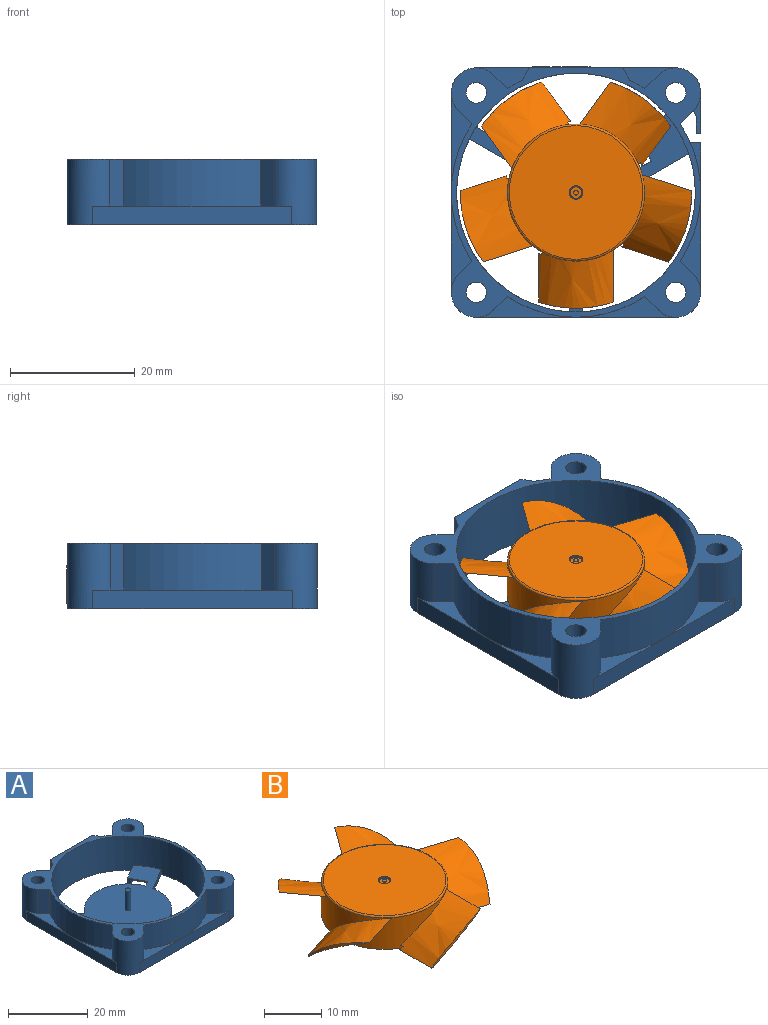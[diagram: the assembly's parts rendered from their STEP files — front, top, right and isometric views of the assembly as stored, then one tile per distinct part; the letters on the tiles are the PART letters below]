
ASSEMBLY  parts=2 mates=1
PART A: 78 faces, bbox 40x40.2x10.5 mm
  f0: plane 32x10.5mm, normal (0,1,0), area 191.9mm2, adj f9,f10,f13,f18,f19,f38,f60,f61
  f1: cylinder r=20mm len=7.5mm, axis (0,0,-1), area 20.7mm2, adj f10,f29,f38,f60
  f2: plane 35.21x31.71mm, normal (0,0,1), area 463mm2, adj f25,f39,f40,f41,f42,f43,f44,f45
  f3: plane 7.98x1.66mm, normal (0,0,1), area 4.3mm2, adj f4,f27,f54
  f4: plane 23.98x3mm, normal (1,0,0), area 71.9mm2, adj f3,f11,f13,f16,f54
  f5: plane 16x3.32mm, normal (0,0,1), area 17.6mm2, adj f15,f16,f36,f37
  f6: plane 16x3.32mm, normal (0,0,1), area 17.6mm2, adj f14,f15,f35,f36
  f7: plane 16x3.32mm, normal (0,0,1), area 17.6mm2, adj f14,f20,f33,f34
  f8: plane 16x3.32mm, normal (0,0,1), area 17.6mm2, adj f19,f20,f32,f33
  f9: plane 8.5x3.32mm, normal (0,0,1), area 13.2mm2, adj f0,f19,f30,f31,f61
  f10: plane 8.5x3.32mm, normal (0,0,1), area 13.2mm2, adj f0,f1,f18,f29,f60
  f11: plane 16x3.32mm, normal (0,0,1), area 17.6mm2, adj f4,f16,f26,f27
  f12: plane 6.52x1.17mm, normal (0,0,1), area 3.8mm2, adj f17,f18,f55,f56,f57
  f13: plane 40x40mm, normal (0,0,-1), area 825.1mm2, adj f0,f4,f14,f15,f16,f17,f18,f19
  f14: cylinder r=4mm len=10.5mm, axis (0,0,-1), area 113.1mm2, adj f6,f7,f13,f15,f20,f34,f35,f38
  f15: plane 32x3mm, normal (0,-1,0), area 96mm2, adj f5,f6,f13,f14,f16
  f16: cylinder r=4mm len=10.5mm, axis (0,0,-1), area 113.1mm2, adj f4,f5,f11,f13,f15,f26,f37,f38
  f17: plane 6.52x3mm, normal (1,0,0), area 19.6mm2, adj f12,f13,f18,f55
  f18: cylinder r=4mm len=10.5mm, axis (0,0,-1), area 113.1mm2, adj f0,f10,f12,f13,f17,f28,f29,f38
  f19: cylinder r=4mm len=10.5mm, axis (0,0,-1), area 113.1mm2, adj f0,f8,f9,f13,f20,f31,f32,f38
  f20: plane 32x3mm, normal (-1,0,0), area 96mm2, adj f7,f8,f13,f14,f19
  f21: cylinder r=1.65mm len=10.5mm, axis (0,0,-1), area 108.9mm2, adj f13,f38
  f22: cylinder r=1.65mm len=10.5mm, axis (0,0,-1), area 108.9mm2, adj f13,f38
  f23: cylinder r=1.65mm len=10.5mm, axis (0,0,-1), area 108.9mm2, adj f13,f38
  f24: cylinder r=1.65mm len=10.5mm, axis (0,0,-1), area 108.9mm2, adj f13,f38
  f25: cylinder r=19.15mm len=38.3mm, axis (0,0,-1), area 1245.8mm2, adj f2,f13,f38,f40,f41,f43,f44,f46
  f26: plane 7.5x2.14mm, normal (0.71,0.71,0), area 22.7mm2, adj f11,f16,f27,f38
  f27: cylinder r=20mm len=22.06mm, axis (0,0,-1), area 181.8mm2, adj f3,f11,f26,f28,f38,f53,f54
  f28: plane 10.5x2.14mm, normal (0.71,-0.71,0), area 31.8mm2, adj f13,f18,f27,f38,f51,f57
  f29: plane 7.5x2.14mm, normal (-0.71,0.71,0), area 22.7mm2, adj f1,f10,f18,f38
  f30: cylinder r=20mm len=7.5mm, axis (0,0,-1), area 20.7mm2, adj f9,f31,f38,f61
  f31: plane 7.5x2.14mm, normal (0.71,0.71,0), area 22.7mm2, adj f9,f19,f30,f38
  f32: plane 7.5x2.14mm, normal (-0.71,-0.71,0), area 22.7mm2, adj f8,f19,f33,f38
  f33: cylinder r=20mm len=22.06mm, axis (0,0,-1), area 175.2mm2, adj f7,f8,f32,f34,f38
  f34: plane 7.5x2.14mm, normal (-0.71,0.71,0), area 22.7mm2, adj f7,f14,f33,f38
  f35: plane 7.5x2.14mm, normal (0.71,-0.71,0), area 22.7mm2, adj f6,f14,f36,f38
  f36: cylinder r=20mm len=22.06mm, axis (0,0,-1), area 175.2mm2, adj f5,f6,f35,f37,f38
  f37: plane 7.5x2.14mm, normal (-0.71,-0.71,0), area 22.7mm2, adj f5,f16,f36,f38
  f38: plane 40x40mm, normal (0,0,1), area 268.1mm2, adj f0,f1,f14,f16,f18,f19,f21,f22
  f39: cylinder r=11mm len=15.46mm, axis (0,0,-1), area 31.3mm2, adj f2,f13,f40,f47
  f40: plane 8.17x1.5mm, normal (-1,0,0), area 12.3mm2, adj f2,f13,f25,f39
  f41: plane 8.17x1.5mm, normal (1,0,0), area 12.3mm2, adj f2,f13,f25,f42
  f42: cylinder r=11mm len=12.97mm, axis (0,0,-1), area 27.3mm2, adj f2,f13,f41,f43
  f43: plane 7.29x4.21mm, normal (0.5,-0.87,0), area 12.6mm2, adj f2,f13,f25,f42
  f44: plane 5.02x2.9mm, normal (-0.5,0.87,0), area 8.7mm2, adj f2,f13,f25,f49
  f45: cylinder r=11mm len=19.17mm, axis (0,0,-1), area 35.4mm2, adj f2,f13,f46,f48
  f46: plane 7.08x4.09mm, normal (0.5,0.87,0), area 12.3mm2, adj f2,f13,f25,f45
  f47: plane 7.08x4.09mm, normal (-0.5,-0.87,0), area 12.3mm2, adj f2,f13,f25,f39
  f48: plane 6.86x3.96mm, normal (-0.5,0.87,0), area 9.6mm2, adj f2,f13,f45,f49,f50,f53
  f49: plane 4.59x2.65mm, normal (-0.87,-0.5,0), area 3.2mm2, adj f2,f13,f44,f48,f52,f53
  f50: plane 1.23x1.1mm, normal (-0.01,1,0), area 1.4mm2, adj f13,f48,f53,f54
  f51: cylinder r=20mm len=1.18mm, axis (0,0,-1), area 1.6mm2, adj f13,f28,f52,f53
  f52: plane 5.91x3.41mm, normal (0.5,-0.87,0), area 7.5mm2, adj f13,f49,f51,f53
  f53: plane 8.41x7.14mm, normal (0,0,-1), area 30.3mm2, adj f27,f48,f49,f50,f51,f52
  f54: plane 3x1.66mm, normal (0,1,0), area 5mm2, adj f3,f4,f13,f27,f50
  f55: plane 3x0.7mm, normal (0,-1,0), area 2.1mm2, adj f12,f13,f17,f56
  f56: plane 3x2.73mm, normal (-1,0,0), area 8.2mm2, adj f12,f13,f55,f57
  f57: plane 3x0.96mm, normal (-0.9,-0.44,0), area 3.2mm2, adj f12,f13,f28,f56
  f58: cylinder r=0.75mm len=6mm, axis (0,0,-1), area 28.3mm2, adj f2,f59
  f59: plane 1.5x1.5mm, normal (0,0,1), area 1.8mm2, adj f58
  f60: plane 7.5x1.96mm, normal (0.87,0.5,0), area 17mm2, adj f0,f1,f10,f38
  f61: plane 7.5x1.96mm, normal (-0.87,0.5,0), area 17mm2, adj f0,f9,f30,f38
  f62: plane 1.4x0.2mm, normal (1,0,0), area 0.3mm2, adj f0,f63,f68,f69
  f63: plane 4x0.2mm, normal (0,0,-1), area 0.8mm2, adj f0,f62,f64,f69
  f64: plane 0.65x0.2mm, normal (1,0,0), area 0.1mm2, adj f0,f63,f65,f69
  f65: plane 2x1.35mm, normal (-0.56,0,-0.83), area 0.5mm2, adj f0,f64,f66,f69
  f66: plane 2x1.35mm, normal (-0.56,0,0.83), area 0.5mm2, adj f0,f65,f67,f69
  f67: plane 0.65x0.2mm, normal (1,0,0), area 0.1mm2, adj f0,f66,f68,f69
  f68: plane 4x0.2mm, normal (0,0,1), area 0.8mm2, adj f0,f62,f67,f69
  f69: plane 6x2.7mm, normal (0,1,0), area 8.3mm2, adj f62,f63,f64,f65,f66,f67,f68
  f70: plane 1.4x0.2mm, normal (0,0,1), area 0.3mm2, adj f0,f71,f76,f77
  f71: plane 4x0.2mm, normal (1,0,0), area 0.8mm2, adj f0,f70,f72,f77
  f72: plane 0.65x0.2mm, normal (0,0,1), area 0.1mm2, adj f0,f71,f73,f77
  f73: plane 2x1.35mm, normal (0.83,0,-0.56), area 0.5mm2, adj f0,f72,f74,f77
  f74: plane 2x1.35mm, normal (-0.83,0,-0.56), area 0.5mm2, adj f0,f73,f75,f77
  f75: plane 0.65x0.2mm, normal (0,0,1), area 0.1mm2, adj f0,f74,f76,f77
  f76: plane 4x0.2mm, normal (-1,0,0), area 0.8mm2, adj f0,f70,f75,f77
  f77: plane 6x2.7mm, normal (0,1,0), area 8.3mm2, adj f70,f71,f72,f73,f74,f75,f76
PART B: 45 faces, bbox 39x37.1x7 mm
  f0: plane 1.8x1.8mm, normal (0,0,1), area 2mm2, adj f32,f43
  f1: plane 22x22mm, normal (0,0,-1), area 66mm2, adj f6,f25
  f2: plane 7.66x2.66mm, normal (0,0,-1), area 2.3mm2, adj f12,f13,f14,f40
  f3: plane 6.62x4.76mm, normal (0,0,-1), area 2.3mm2, adj f15,f16,f17,f38
  f4: plane 6.39x4.92mm, normal (0,0,-1), area 2.3mm2, adj f18,f19,f20,f36
  f5: plane 7.48x2.75mm, normal (0,0,-1), area 2.3mm2, adj f21,f22,f23,f34
  f6: cylinder r=11mm len=22mm, axis (0,0,-1), area 435.1mm2, adj f1,f9,f10,f13,f14,f16,f17,f19
  f7: plane 21.4x21.4mm, normal (0,0,1), area 355.9mm2, adj f30,f31
  f8: plane 7.96x0.3mm, normal (0,0,-1), area 2.3mm2, adj f9,f10,f11,f41
  f9: extruded ~12x9.33mm, area 109.9mm2, adj f6,f8,f10,f11,f41,f42
  f10: extruded ~11.7x9.33mm, area 105.8mm2, adj f6,f8,f9,f11,f41,f42
  f11: cylinder r=18.55mm len=12mm, axis (0,0,-1), area 5.7mm2, adj f8,f9,f10
  f12: cylinder r=18.55mm len=11.41mm, axis (0,0,-1), area 5.7mm2, adj f2,f13,f14
  f13: extruded ~14.01x12.49mm, area 105.8mm2, adj f2,f6,f12,f14,f39,f40
  f14: extruded ~14.3x12.58mm, area 109.9mm2, adj f2,f6,f12,f13,f39,f40
  f15: cylinder r=18.55mm len=9.71mm, axis (0,0,-1), area 5.7mm2, adj f3,f16,f17
  f16: extruded ~14.95x14.43mm, area 105.8mm2, adj f3,f6,f15,f17,f37,f38
  f17: extruded ~15.19x14.6mm, area 109.9mm2, adj f3,f6,f15,f16,f37,f38
  f18: cylinder r=18.55mm len=9.71mm, axis (0,0,-1), area 5.7mm2, adj f4,f19,f20
  f19: extruded ~14.95x14.43mm, area 105.8mm2, adj f4,f6,f18,f20,f35,f36
  f20: extruded ~15.19x14.6mm, area 109.9mm2, adj f4,f6,f18,f19,f35,f36
  f21: extruded ~14.3x12.58mm, area 109.9mm2, adj f5,f6,f22,f23,f33,f34
  f22: extruded ~14.01x12.49mm, area 105.8mm2, adj f5,f6,f21,f23,f33,f34
  f23: cylinder r=18.55mm len=11.41mm, axis (0,0,-1), area 5.7mm2, adj f5,f21,f22
  f24: cylinder r=1.75mm len=5.5mm, axis (0,0,-1), area 60.5mm2, adj f26,f27
  f25: cylinder r=10mm len=20mm, axis (0,0,-1), area 345.6mm2, adj f1,f26
  f26: plane 20x20mm, normal (0,0,-1), area 304.5mm2, adj f24,f25
  f27: plane 3.5x3.5mm, normal (0,0,-1), area 7.9mm2, adj f24,f28
  f28: cylinder r=0.75mm len=5.5mm, axis (0,0,-1), area 25.9mm2, adj f27,f29
  f29: plane 1.5x1.5mm, normal (0,0,-1), area 1.8mm2, adj f28
  f30: torus R=10.7mm, axis (0,0,1), area 32.2mm2, adj f6,f7
  f31: torus R=1.1mm, axis (0,0,1), area 1mm2, adj f7,f32
  f32: torus R=0.9mm, axis (0,0,1), area 1mm2, adj f0,f31
  f33: plane 0.6x0.52mm, normal (0,0,-1), area 0.2mm2, adj f6,f21,f22,f34
  f34: cylinder r=11.4mm len=1.01mm, axis (0,0,-1), area 0.2mm2, adj f5,f21,f22,f33
  f35: plane 0.73x0.43mm, normal (0,0,-1), area 0.2mm2, adj f6,f19,f20,f36
  f36: cylinder r=11.4mm len=1.02mm, axis (0,0,-1), area 0.2mm2, adj f4,f19,f20,f35
  f37: plane 0.79x0.47mm, normal (0,0,-1), area 0.2mm2, adj f6,f16,f17,f38
  f38: cylinder r=11.4mm len=0.94mm, axis (0,0,-1), area 0.2mm2, adj f3,f16,f17,f37
  f39: plane 0.77x0.46mm, normal (0,0,-1), area 0.2mm2, adj f6,f13,f14,f40
  f40: cylinder r=11.4mm len=0.76mm, axis (0,0,-1), area 0.2mm2, adj f2,f13,f14,f39
  f41: cylinder r=11.4mm len=0.9mm, axis (0,0,-1), area 0.2mm2, adj f8,f9,f10,f42
  f42: plane 0.68x0.41mm, normal (0,0,-1), area 0.2mm2, adj f6,f9,f10,f41
  f43: cylinder r=0.4mm len=0.8mm, axis (0,0,-1), area 0.3mm2, adj f0,f44
  f44: plane 0.8x0.8mm, normal (0,0,1), area 0.5mm2, adj f43
PLACE A at identity
PLACE B t=(0,0,1.5)mm
MATE fastened B.f6 <-> A.f58  axis (0,0,-1) through (0,0,1.5)mm
